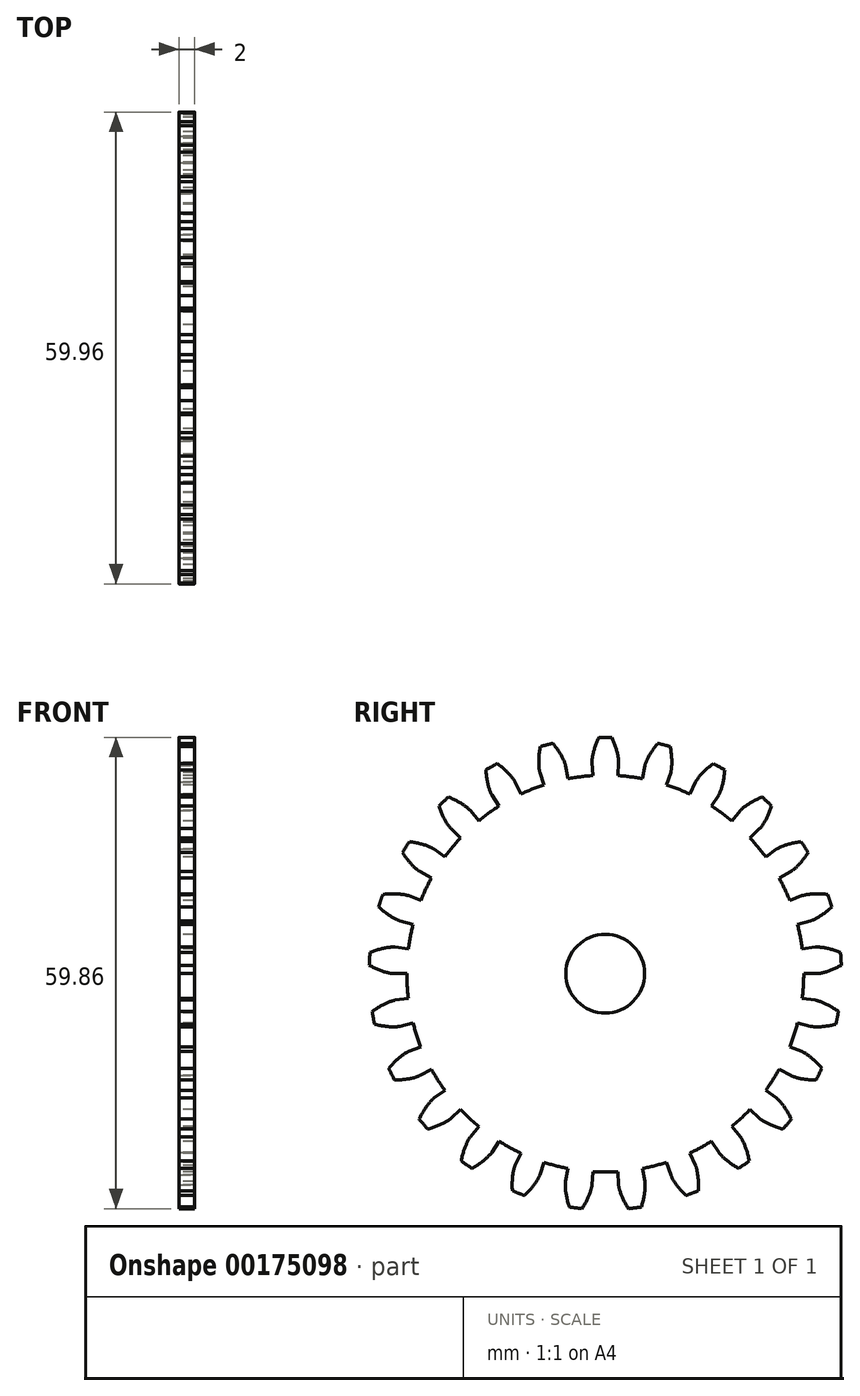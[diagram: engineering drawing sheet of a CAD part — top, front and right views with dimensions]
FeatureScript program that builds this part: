
annotation { "Feature Type Name" : "Feature", "Feature Type Description" : "" }
export const myFeature = defineFeature(function(context is Context, id is Id, definition is map)
    precondition{}
    {
        {
            assignVariable(context, id + "F0", {"name" : "NumberTeeth", "anyValue" : 25});
        }
        {
            assignVariable(context, id + "F1", {"name" : "GearThickness", "anyValue" : 2});
        }
        {
            var Q0;
            Q0=qCreatedBy(makeId("Right.planeOp"),FACE);
            var sketch = newSketch(context, id + "F2", { "sketchPlane" : qUnion([Q0])});
            skCircle(sketch, "E0", {"center": v(0, 0) * mm, "radius": 25.2 * mm});
            skCircle(sketch, "E1", {"center": v(0, 0) * mm, "radius": 26.9 * mm, "construction": true});
            skCircle(sketch, "E2", {"center": v(0, 0) * mm, "radius": 27.78 * mm, "construction": true});
            skCircle(sketch, "E3", {"center": v(0, 0) * mm, "radius": 30 * mm});
            skLineSegment(sketch, "E4", {"start": v(0, 0) * mm, "end": v(-26.9, 0) * mm, "construction": true});
            skLineSegment(sketch, "E5.1.0", {"start": v(0, 0) * mm, "end": v(-26.86, 1.34) * mm, "construction": true});
            skLineSegment(sketch, "E5.2.0", {"start": v(0, 0) * mm, "end": v(-26.76, 2.68) * mm, "construction": true});
            skLineSegment(sketch, "E5.3.0", {"start": v(0, 0) * mm, "end": v(-26.6, 4.02) * mm, "construction": true});
            skLineSegment(sketch, "E5.4.0", {"start": v(0, 0) * mm, "end": v(-26.36, 5.34) * mm, "construction": true});
            skLineSegment(sketch, "E5.5.0", {"start": v(0, 0) * mm, "end": v(-26.06, 6.65) * mm, "construction": true});
            skLineSegment(sketch, "E5.6.0", {"start": v(0, 0) * mm, "end": v(-25.7, 7.95) * mm, "construction": true});
            skLineSegment(sketch, "E5.7.0", {"start": v(0, 0) * mm, "end": v(-25.26, 9.22) * mm, "construction": true});
            skLineSegment(sketch, "E5.8.0", {"start": v(0, 0) * mm, "end": v(-24.77, 10.47) * mm, "construction": true});
            skLineSegment(sketch, "E5.9.0", {"start": v(0, 0) * mm, "end": v(-24.22, 11.7) * mm, "construction": true});
            skLineSegment(sketch, "E5.10.0", {"start": v(0, 0) * mm, "end": v(-23.6, 12.9) * mm, "construction": true});
            skLineSegment(sketch, "E5.11.0", {"start": v(0, 0) * mm, "end": v(-22.93, 14.06) * mm, "construction": true});
            skLineSegment(sketch, "E5.12.0", {"start": v(0, 0) * mm, "end": v(-22.2, 15.18) * mm, "construction": true});
            skLineSegment(sketch, "E5.13.0", {"start": v(0, 0) * mm, "end": v(-21.4, 16.28) * mm, "construction": true});
            skLineSegment(sketch, "E5.14.0", {"start": v(0, 0) * mm, "end": v(-20.57, 17.32) * mm, "construction": true});
            skLineSegment(sketch, "E5.anchor2", {"start": v(0, 0) * mm, "end": v(-20.57, 17.32) * mm, "construction": true});
            skLineSegment(sketch, "E6", {"start": v(-26.86, 1.34) * mm, "end": v(-26.93, 0) * mm, "construction": true});
            skLineSegment(sketch, "E7", {"start": v(-26.76, 2.68) * mm, "end": v(-27.03, 0) * mm, "construction": true});
            skLineSegment(sketch, "E8", {"start": v(-26.6, 4.02) * mm, "end": v(-27.2, 0.03) * mm, "construction": true});
            skLineSegment(sketch, "E9", {"start": v(-26.06, 6.65) * mm, "end": v(-27.72, 0.14) * mm, "construction": true});
            skLineSegment(sketch, "E10", {"start": v(-25.7, 7.95) * mm, "end": v(-28.08, 0.24) * mm, "construction": true});
            skLineSegment(sketch, "E11", {"start": v(-25.26, 9.22) * mm, "end": v(-28.5, 0.38) * mm, "construction": true});
            skLineSegment(sketch, "E12", {"start": v(-24.77, 10.47) * mm, "end": v(-28.96, 0.56) * mm, "construction": true});
            skLineSegment(sketch, "E13", {"start": v(-24.22, 11.7) * mm, "end": v(-29.48, 0.8) * mm, "construction": true});
            skLineSegment(sketch, "E14", {"start": v(-23.6, 12.9) * mm, "end": v(-30.05, 1.1) * mm, "construction": true});
            skLineSegment(sketch, "E15", {"start": v(-22.93, 14.06) * mm, "end": v(-30.66, 1.45) * mm, "construction": true});
            skLineSegment(sketch, "E16", {"start": v(-26.36, 5.34) * mm, "end": v(-27.43, 0.07) * mm, "construction": true});
            skLineSegment(sketch, "E17", {"start": v(-22.2, 15.18) * mm, "end": v(-31.3, 1.87) * mm, "construction": true});
            skLineSegment(sketch, "E18", {"start": v(-21.4, 16.28) * mm, "end": v(-31.99, 2.36) * mm, "construction": true});
            skLineSegment(sketch, "E19", {"start": v(-20.57, 17.32) * mm, "end": v(-32.7, 2.93) * mm, "construction": true});
            skLineSegment(sketch, "E20", {"start": v(0, 0) * mm, "end": v(-26.84, 1.69) * mm, "construction": true});
            skLineSegment(sketch, "E21", {"start": v(-25.2, 0) * mm, "end": v(-26.9, 0) * mm});
            skLineSegment(sketch, "E22.MirrorCS", {"start": v(-25, 3.16) * mm, "end": v(-26.68, 3.37) * mm});
            skLineSegment(sketch, "E23", {"start": v(-13.28, -13.43) * mm, "end": v(-32.7, 2.93) * mm, "construction": true});
            skFitSpline(sketch, "E24", {"points": [v(-32.7, 2.93) * mm, v(-31.99, 2.36) * mm, v(-31.3, 1.87) * mm, v(-30.66, 1.45) * mm, v(-30.05, 1.1) * mm, v(-29.48, 0.8) * mm, v(-28.96, 0.56) * mm, v(-28.5, 0.38) * mm, v(-28.08, 0.24) * mm, v(-27.72, 0.14) * mm, v(-27.43, 0.07) * mm, v(-27.2, 0.03) * mm, v(-27.03, 0) * mm, v(-26.93, 0) * mm, v(-26.9, 0) * mm], "startDerivative": vector(0.19, -0.16) * mm, "endDerivative": vector(0.04, 0) * mm});
            skFitSpline(sketch, "E25.MirrorCS", {"points": [v(-32.8, 1.2) * mm, v(-32.03, 1.67) * mm, v(-31.3, 2.07) * mm, v(-30.6, 2.4) * mm, v(-29.95, 2.68) * mm, v(-29.35, 2.9) * mm, v(-28.8, 3.07) * mm, v(-28.31, 3.2) * mm, v(-27.88, 3.28) * mm, v(-27.52, 3.34) * mm, v(-27.22, 3.37) * mm, v(-26.98, 3.38) * mm, v(-26.82, 3.38) * mm, v(-26.71, 3.37) * mm, v(-26.68, 3.37) * mm], "startDerivative": vector(0.2, 0.13) * mm, "endDerivative": vector(0.04, 0) * mm});
            skCircle(sketch, "E26", {"center": v(0, 0) * mm, "radius": 5 * mm});
            skSolve(sketch);
        }
        {
            var Q0;
            {var subQ0=sQuery(id+"F2.wireOp",EDGE,"E0");var subQ1=makeQuery(id+"F2.imprint","INTERSECT",VERTEX,{"derivedFrom":[subQ0,sQuery(id+"F2.wireOp",EDGE,"E21")]});Q0=makeQuery(id+"F2.imprint","IMPRINT",FACE,{"disambiguationData":[TD([[makeQuery(id+"F2.imprint","IMPRINT",EDGE,{"disambiguationData":[TD([[subQ1,1.0]])],"derivedFrom":subQ0}),1.0]])]});}
            extrude(context, id + "F3", {"entities" : qUnion([Q0]), "depth" : (getVariable(context, 'GearThickness')) * mm});
        }
        {
            var Q0;
            {var subQ1=sQuery(id+"F2.wireOp",EDGE,"E21");Q0=makeQuery(id+"F2.imprint","IMPRINT",FACE,{"disambiguationData":[TD([[makeQuery(id+"F2.imprint","IMPRINT",EDGE,{"derivedFrom":subQ1}),-1.0]])]});}
            extrude(context, id + "F4", {"entities" : qUnion([Q0]), "depth" : (getVariable(context, 'GearThickness')) * mm});
        }
        {
            var Q0;
            Q0=makeQuery(id+"F4.opExtrude","SWEPT_BODY",BODY,{"disambiguationData":[OSD([sQuery(id+"F2.wireOp",EDGE,"E0"),sQuery(id+"F2.wireOp",EDGE,"E3"),sQuery(id+"F2.wireOp",EDGE,"E21"),sQuery(id+"F2.wireOp",EDGE,"E22.MirrorCS"),sQuery(id+"F2.wireOp",EDGE,"E24"),sQuery(id+"F2.wireOp",EDGE,"E25.MirrorCS")])]});
            var Q1;
            Q1=makeQuery(id+"F3.opExtrude","SWEPT_FACE",FACE,{"disambiguationData":[OSD([sQuery(id+"F2.wireOp",EDGE,"abc1c1ef-9107-4900-9671-dac890a315ee0.MirrorCS")])]});
            var Q2;
            Q2=makeQuery(id+"F3.opExtrude","SWEPT_FACE",FACE,{"disambiguationData":[OSD([sQuery(id+"F2.wireOp",EDGE,"33001111-3cf2-4703-a9ad-cefdc3e51004")])]});
            var Q3;
            Q3=makeQuery(id+"F3.opExtrude","SWEPT_FACE",FACE,{"disambiguationData":[OSD([sQuery(id+"F2.wireOp",EDGE,"E3")])]});
            var Q4;
            Q4=makeQuery(id+"F3.opExtrude","SWEPT_FACE",FACE,{"disambiguationData":[OSD([sQuery(id+"F2.wireOp",EDGE,"E22.MirrorCS")])]});
            var Q5;
            Q5=makeQuery(id+"F3.opExtrude","SWEPT_FACE",FACE,{"disambiguationData":[OSD([sQuery(id+"F2.wireOp",EDGE,"E21")])]});
            var Q6;
            Q6=makeQuery(id+"F3.opExtrude","SWEPT_FACE",FACE,{"disambiguationData":[OSD([sQuery(id+"F2.wireOp",EDGE,"E0")])]});
            circularPattern(context, id + "F5", {"operationType" : NewBodyOperationType.ADD, "entities" : qUnion([Q0]), "axis" : qUnion([Q6]), "angle" : 360 * degree, "instanceCount" : getVariable(context, 'NumberTeeth'), "equalSpace" : true});
        }
    });
